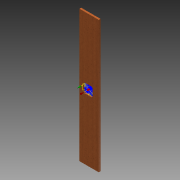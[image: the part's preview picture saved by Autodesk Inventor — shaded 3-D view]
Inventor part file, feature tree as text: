
AUTODESK INVENTOR PART (.ipt)
format: ipt  version: 2015 SP1 (Build 190203100, 203)  size: 184,832 bytes
history: native  units: in
note: dims shown in document units (in); Inventor stores cm internally (conversion verified against a paired STEP export)
features: reference x8, extrude x3, sketch x3, projected_geometry x2
ambient origin geometry x8: Origin, YZ Plane, XZ Plane, XY Plane, X Axis, Y Axis, Z Axis, Center Point
bodies: Solid1 (feature_tree)
feature tree (16):
  extrude  "Extrusion1"  Depth=0.315in
  extrude  "Extrusion2"  Depth=0.3543in TaperAngle=0.0deg
  extrude  "Extrusion3"  [1 undecoded]
  sketch  "Sketch1"  dims[d0=0.315in d1=0.0in d2=0.3465in]
  reference  "Reference1"
  reference  "Reference2"
  reference  "Reference3"
  reference  "Reference4"
  reference  "Reference5"
  reference  "Reference6"
  reference  "Reference7"
  reference  "Reference8"
  sketch  "Sketch2"  dims[d3=0.7461in d4=0.3543in d5=0.0in]
  projected_geometry  "Projected Loop1"
  sketch  "Sketch3"  dims[d6=0.3543in d7=0.0in]
  projected_geometry  "Projected Loop2"
note: 1 required parameter value undecoded (feature->parameter linkage not recoverable at this tier; creation-order binding heuristic only, values carry confidence <= 0.55)
